# Revit family: 756-102-152-DN150-600
name_source: partatom
category: Pipe Accessories
units: mm (PartAtom-declared; Revit-internal decimal feet)

## family parameters
Always vertical = Yes
Cut with Voids When Loaded = No
Part Type = Valve - Breaks Into
Round Connector Dimension = Use Diameter
Shared = No
Work Plane-Based = No

## types (17) — shared parameters
Body_wallthickness = 10 mm  [stored 0.0328084 ft]
DN150_PN10/16 = 756-0150-1-14102
DN200_PN10 = 756-0200-1-04102
DN200_PN16 = 756-0200-1-14102
DN250_PN10 = 756-0250-1-04102
DN250_PN16 = 756-0250-1-14102
DN300_PN10 = 756-0300-1-04102
DN300_PN16 = 756-0300-1-14102
DN350_PN10 = 756-0350-1-04102
DN350_PN16 = 756-0350-1-14102
DN400_PN10 = 756-0400-1-04102
DN400_PN16 = 756-0400-1-14102
DN450_PN10 = 756-0450-1-04102
DN450_PN16 = 756-0450-1-14102
DN500_PN10 = 756-0500-1-04102
DN500_PN16 = 756-0500-1-14102
DN600_PN10 = 756-0600-1-04102
DN600_PN16 = 756-0600-1-14102
Description_ = AVK DOUBLE ECC. BUTTERFLY VALVE, LONG
GB_Flange = 5 mm  [stored 0.0164042 ft]
Pin_dia = 30 mm  [stored 0.0984252 ft]
RF_Cut_Thickness = 5 mm  [stored 0.0164042 ft]
Rib_depth = 15 mm  [stored 0.0492126 ft]
Search_table = 756-102-152-DN150-600
URL_product_pages = https://www.avkvalves.com

## per-type parameters (varying)
- DN150-PN10/16: A=118 mm; B=224 mm; Bottom_Depth=225 mm; Bottom_width=120 mm; C=181 mm; C_rod=9 mm  [stored 0.0295276 ft]; D1=7.5 mm  [stored 0.0246063 ft]; DN=150 mm; Disc_1=2 mm  [stored 0.00656168 ft]; Disc_2=2 mm  [stored 0.00656168 ft]; Disc_Dia=133 mm; Disc_width=10 mm  [stored 0.0328084 ft]; Flange_OD=142.5 mm; Flange_Thickness=15 mm  [stored 0.0492126 ft]; GB_Dia=35 mm  [stored 0.114829 ft]; GB_Width=76 mm; GB_Width_2=76.5 mm; GB_Width_3=85 mm; Gear_box_Mount_Flange_width=50 mm; Gear_box_Mount_width=43 mm  [stored 0.141076 ft]; Gear_box_depth=83 mm; Gear_box_width=33.5 mm; H1=189 mm; H2=201 mm; H3=230 mm; ID (Radius)=75 mm; L=210 mm; L1=1 mm  [stored 0.00328084 ft]; L2=1 mm  [stored 0.00328084 ft]; Pin_Depth=217.5 mm; Pin_width=105 mm; Rf_Dia=105.5 mm; Rib_height=129.55 mm; Rib_height_2=46.5 mm  [stored 0.152559 ft]; Rib_width=180 mm; Rib_width_2=100 mm; W1=155 mm; W2=287 mm; W3=6 mm  [stored 0.019685 ft]; W4=6 mm  [stored 0.019685 ft]; W5=158 mm; offset=3 mm  [stored 0.00984252 ft]
- DN200_PN10: A=118 mm; B=245 mm; Bottom_Depth=300.15 mm; Bottom_width=140 mm; C=191 mm; C_rod=14 mm  [stored 0.0459318 ft]; D1=7.5 mm  [stored 0.0246063 ft]; DN=200.1 mm; Disc_1=2 mm  [stored 0.00656168 ft]; Disc_2=2 mm  [stored 0.00656168 ft]; Disc_Dia=180 mm; Disc_width=15 mm  [stored 0.0492126 ft]; Flange_OD=170 mm; Flange_Thickness=15 mm  [stored 0.0492126 ft]; GB_Dia=35 mm  [stored 0.114829 ft]; GB_Width=76 mm; GB_Width_2=76.5 mm; GB_Width_3=85 mm; Gear_box_Mount_Flange_width=50 mm; Gear_box_Mount_width=43 mm  [stored 0.141076 ft]; Gear_box_depth=83 mm; Gear_box_width=19.5 mm  [stored 0.0639764 ft]; H1=210 mm; H2=227 mm; H3=240 mm; ID (Radius)=100.05 mm; L=230 mm; L1=1 mm  [stored 0.00328084 ft]; L2=1 mm  [stored 0.00328084 ft]; Pin_Depth=270.05 mm; Pin_width=115 mm; Rf_Dia=133 mm; Rib_height=154.55 mm; Rib_height_2=40 mm  [stored 0.131234 ft]; Rib_width=200 mm; Rib_width_2=100 mm; W1=182 mm; W2=308 mm; W3=6 mm  [stored 0.019685 ft]; W4=6 mm  [stored 0.019685 ft]; W5=158 mm; offset=5 mm  [stored 0.0164042 ft]
- DN200_PN16: A=118 mm; B=245 mm; Bottom_Depth=300.24 mm; Bottom_width=140 mm; C=191 mm; C_rod=14 mm  [stored 0.0459318 ft]; D1=7.5 mm  [stored 0.0246063 ft]; DN=200.16 mm; Disc_1=2 mm  [stored 0.00656168 ft]; Disc_2=2 mm  [stored 0.00656168 ft]; Disc_Dia=180 mm; Disc_width=15 mm  [stored 0.0492126 ft]; Flange_OD=170 mm; Flange_Thickness=15 mm  [stored 0.0492126 ft]; GB_Dia=35 mm  [stored 0.114829 ft]; GB_Width=76 mm; GB_Width_2=76.5 mm; GB_Width_3=85 mm; Gear_box_Mount_Flange_width=50 mm; Gear_box_Mount_width=43 mm  [stored 0.141076 ft]; Gear_box_depth=83 mm; Gear_box_width=28.5 mm  [stored 0.0935039 ft]; H1=210 mm; H2=227 mm; H3=250 mm; ID (Radius)=100.08 mm; L=230 mm; L1=1 mm  [stored 0.00328084 ft]; L2=1 mm  [stored 0.00328084 ft]; Pin_Depth=270.08 mm; Pin_width=115 mm; Rf_Dia=133 mm; Rib_height=154.55 mm; Rib_height_2=40 mm  [stored 0.131234 ft]; Rib_width=200 mm; Rib_width_2=100 mm; W1=182 mm; W2=308 mm; W3=6 mm  [stored 0.019685 ft]; W4=6 mm  [stored 0.019685 ft]; W5=158 mm; offset=5 mm  [stored 0.0164042 ft]
- DN250_PN10: A=118 mm; B=279 mm; Bottom_Depth=375.15 mm; Bottom_width=170 mm; C=201 mm; C_rod=14 mm  [stored 0.0459318 ft]; D1=7.5 mm  [stored 0.0246063 ft]; DN=250.1 mm; Disc_1=2 mm  [stored 0.00656168 ft]; Disc_2=2 mm  [stored 0.00656168 ft]; Disc_Dia=227 mm; Disc_width=15 mm  [stored 0.0492126 ft]; Flange_OD=202.5 mm; Flange_Thickness=15 mm  [stored 0.0492126 ft]; GB_Dia=35 mm  [stored 0.114829 ft]; GB_Width=76 mm; GB_Width_2=76.5 mm; GB_Width_3=85 mm; Gear_box_Mount_Flange_width=45 mm  [stored 0.147638 ft]; Gear_box_Mount_width=37 mm  [stored 0.121391 ft]; Gear_box_depth=83 mm; Gear_box_width=19.5 mm  [stored 0.0639764 ft]; H1=244 mm; H2=261 mm; H3=260 mm; ID (Radius)=125.05 mm; L=250 mm; L1=1 mm  [stored 0.00328084 ft]; L2=1 mm  [stored 0.00328084 ft]; Pin_Depth=327.55 mm; Pin_width=125 mm; Rf_Dia=159.5 mm; Rib_height=184.09 mm; Rib_height_2=41.5 mm  [stored 0.136155 ft]; Rib_width=220 mm; Rib_width_2=90 mm; W1=215 mm; W2=342 mm; W3=6 mm  [stored 0.019685 ft]; W4=6 mm  [stored 0.019685 ft]; W5=158 mm; offset=5 mm  [stored 0.0164042 ft]
- DN250_PN16: A=118 mm; B=279 mm; Bottom_Depth=375.24 mm; Bottom_width=170 mm; C=201 mm; C_rod=14 mm  [stored 0.0459318 ft]; D1=7.5 mm  [stored 0.0246063 ft]; DN=250.16 mm; Disc_1=2 mm  [stored 0.00656168 ft]; Disc_2=2 mm  [stored 0.00656168 ft]; Disc_Dia=227 mm; Disc_width=15 mm  [stored 0.0492126 ft]; Flange_OD=202.5 mm; Flange_Thickness=15 mm  [stored 0.0492126 ft]; GB_Dia=35 mm  [stored 0.114829 ft]; GB_Width=76 mm; GB_Width_2=76.5 mm; GB_Width_3=85 mm; Gear_box_Mount_Flange_width=45 mm  [stored 0.147638 ft]; Gear_box_Mount_width=37 mm  [stored 0.121391 ft]; Gear_box_depth=83 mm; Gear_box_width=19.5 mm  [stored 0.0639764 ft]; H1=244 mm; H2=261 mm; H3=270 mm; ID (Radius)=125.08 mm; L=250 mm; L1=1 mm  [stored 0.00328084 ft]; L2=1 mm  [stored 0.00328084 ft]; Pin_Depth=327.58 mm; Pin_width=125 mm; Rf_Dia=159.5 mm; Rib_height=184.09 mm; Rib_height_2=41.5 mm  [stored 0.136155 ft]; Rib_width=220 mm; Rib_width_2=90 mm; W1=215 mm; W2=342 mm; W3=6 mm  [stored 0.019685 ft]; W4=6 mm  [stored 0.019685 ft]; W5=158 mm; offset=5 mm  [stored 0.0164042 ft]
- DN300_PN10: A=118 mm; B=309 mm; Bottom_Depth=450.15 mm; Bottom_width=210 mm; C=211 mm; C_rod=19 mm  [stored 0.062336 ft]; D1=7.5 mm  [stored 0.0246063 ft]; DN=300.1 mm; Disc_1=3 mm  [stored 0.00984252 ft]; Disc_2=20 mm  [stored 0.0656168 ft]; Disc_Dia=282.17 mm; Disc_width=20 mm  [stored 0.0656168 ft]; Flange_OD=230 mm; Flange_Thickness=20 mm  [stored 0.0656168 ft]; GB_Dia=35 mm  [stored 0.114829 ft]; GB_Width=76 mm; GB_Width_2=76.5 mm; GB_Width_3=85 mm; Gear_box_Mount_Flange_width=55 mm; Gear_box_Mount_width=45 mm  [stored 0.147638 ft]; Gear_box_depth=83 mm; Gear_box_width=27.5 mm  [stored 0.0902231 ft]; H1=274 mm; H2=292 mm; H3=280 mm; ID (Radius)=150.05 mm; L=270 mm; L1=1 mm  [stored 0.00328084 ft]; L2=12 mm  [stored 0.0393701 ft]; Pin_Depth=380.05 mm; Pin_width=135 mm; Rf_Dia=185 mm; Rib_height=209.09 mm; Rib_height_2=44 mm  [stored 0.144357 ft]; Rib_width=230 mm; Rib_width_2=110 mm; W1=242 mm; W2=373 mm; W3=6 mm  [stored 0.019685 ft]; W4=104 mm; W5=182 mm; offset=6 mm  [stored 0.019685 ft]
- DN300_PN16: A=142 mm; B=314 mm; Bottom_Depth=450.24 mm; Bottom_width=210 mm; C=237 mm; C_rod=19 mm  [stored 0.062336 ft]; D1=8.5 mm  [stored 0.0278871 ft]; DN=300.16 mm; Disc_1=3 mm  [stored 0.00984252 ft]; Disc_2=20 mm  [stored 0.0656168 ft]; Disc_Dia=282.17 mm; Disc_width=20 mm  [stored 0.0656168 ft]; Flange_OD=230 mm; Flange_Thickness=20 mm  [stored 0.0656168 ft]; GB_Dia=35 mm  [stored 0.114829 ft]; GB_Width=102 mm; GB_Width_2=103.5 mm; GB_Width_3=115 mm; Gear_box_Mount_Flange_width=55 mm; Gear_box_Mount_width=45 mm  [stored 0.147638 ft]; Gear_box_depth=107 mm; Gear_box_width=32.5 mm  [stored 0.106627 ft]; H1=279 mm; H2=292 mm; H3=290 mm; ID (Radius)=150.08 mm; L=270 mm; L1=1 mm  [stored 0.00328084 ft]; L2=12 mm  [stored 0.0393701 ft]; Pin_Depth=380.08 mm; Pin_width=135 mm; Rf_Dia=185 mm; Rib_height=209.09 mm; Rib_height_2=49 mm; Rib_width=230 mm; Rib_width_2=110 mm; W1=242 mm; W2=373 mm; W3=6 mm  [stored 0.019685 ft]; W4=104 mm; W5=182 mm; offset=6 mm  [stored 0.019685 ft]
- DN350_PN10: A=118 mm; B=335 mm; Bottom_Depth=525.15 mm; Bottom_width=210 mm; C=221 mm; C_rod=19 mm  [stored 0.062336 ft]; D1=7.5 mm  [stored 0.0246063 ft]; DN=350.1 mm; Disc_1=20 mm  [stored 0.0656168 ft]; Disc_2=20 mm  [stored 0.0656168 ft]; Disc_Dia=334 mm; Disc_width=20 mm  [stored 0.0656168 ft]; Flange_OD=260 mm; Flange_Thickness=20 mm  [stored 0.0656168 ft]; GB_Dia=35 mm  [stored 0.114829 ft]; GB_Width=76 mm; GB_Width_2=76.5 mm; GB_Width_3=85 mm; Gear_box_Mount_Flange_width=60 mm; Gear_box_Mount_width=50 mm; Gear_box_depth=83 mm; Gear_box_width=27 mm  [stored 0.0885827 ft]; H1=300 mm; H2=318 mm; H3=300 mm; ID (Radius)=175.05 mm; L=290 mm; L1=20 mm  [stored 0.0656168 ft]; L2=26 mm; Pin_Depth=435.05 mm; Pin_width=145 mm; Rf_Dia=214.5 mm; Rib_height=236.36 mm; Rib_height_2=40 mm  [stored 0.131234 ft]; Rib_width=250 mm; Rib_width_2=120 mm; W1=272 mm; W2=398 mm; W3=151 mm; W4=173 mm; W5=158 mm; offset=3 mm  [stored 0.00984252 ft]
- DN350_PN16: A=142 mm; B=340 mm; Bottom_Depth=525.24 mm; Bottom_width=210 mm; C=247 mm; C_rod=19 mm  [stored 0.062336 ft]; D1=8.5 mm  [stored 0.0278871 ft]; DN=350.16 mm; Disc_1=20 mm  [stored 0.0656168 ft]; Disc_2=20 mm  [stored 0.0656168 ft]; Disc_Dia=334 mm; Disc_width=20 mm  [stored 0.0656168 ft]; Flange_OD=260 mm; Flange_Thickness=20 mm  [stored 0.0656168 ft]; GB_Dia=35 mm  [stored 0.114829 ft]; GB_Width=102 mm; GB_Width_2=76.5 mm; GB_Width_3=85 mm; Gear_box_Mount_Flange_width=60 mm; Gear_box_Mount_width=50 mm; Gear_box_depth=107 mm; Gear_box_width=32 mm  [stored 0.104987 ft]; H1=305 mm; H2=318 mm; H3=310 mm; ID (Radius)=175.08 mm; L=290 mm; L1=20 mm  [stored 0.0656168 ft]; L2=26 mm; Pin_Depth=435.08 mm; Pin_width=145 mm; Rf_Dia=214.5 mm; Rib_height=236.36 mm; Rib_height_2=45 mm  [stored 0.147638 ft]; Rib_width=250 mm; Rib_width_2=120 mm; W1=272 mm; W2=398 mm; W3=151 mm; W4=173 mm; W5=182 mm; offset=3 mm  [stored 0.00984252 ft]
- DN400_PN10: A=142 mm; B=371 mm; Bottom_Depth=600.15 mm; Bottom_width=260 mm; C=257 mm; C_rod=29 mm  [stored 0.0951444 ft]; D1=8.5 mm  [stored 0.0278871 ft]; DN=400.1 mm; Disc_1=20 mm  [stored 0.0656168 ft]; Disc_2=20 mm  [stored 0.0656168 ft]; Disc_Dia=383 mm; Disc_width=30 mm  [stored 0.0984252 ft]; Flange_OD=290 mm; Flange_Thickness=20 mm  [stored 0.0656168 ft]; GB_Dia=37.5 mm; GB_Width=102 mm; GB_Width_2=76.5 mm; GB_Width_3=85 mm; Gear_box_Mount_Flange_width=55 mm; Gear_box_Mount_width=45 mm  [stored 0.147638 ft]; Gear_box_depth=107 mm; Gear_box_width=32 mm  [stored 0.104987 ft]; H1=333.5 mm; H2=349 mm; H3=320 mm; ID (Radius)=200.05 mm; L=310 mm; L1=35 mm  [stored 0.114829 ft]; L2=41 mm  [stored 0.134514 ft]; Pin_Depth=490.05 mm; Pin_width=155 mm; Rf_Dia=240 mm; Rib_height=263.64 mm; Rib_height_2=43.5 mm  [stored 0.142717 ft]; Rib_width=270 mm; Rib_width_2=110 mm; W1=302 mm; W2=434 mm; W3=215 mm; W4=232 mm; W5=182 mm; offset=3 mm  [stored 0.00984252 ft]
- DN400_PN16: A=142 mm; B=371 mm; Bottom_Depth=600.24 mm; Bottom_width=260 mm; C=257 mm; C_rod=29 mm  [stored 0.0951444 ft]; D1=8.5 mm  [stored 0.0278871 ft]; DN=400.16 mm; Disc_1=20 mm  [stored 0.0656168 ft]; Disc_2=20 mm  [stored 0.0656168 ft]; Disc_Dia=383 mm; Disc_width=30 mm  [stored 0.0984252 ft]; Flange_OD=290 mm; Flange_Thickness=20 mm  [stored 0.0656168 ft]; GB_Dia=37.5 mm; GB_Width=102 mm; GB_Width_2=76.5 mm; GB_Width_3=85 mm; Gear_box_Mount_Flange_width=55 mm; Gear_box_Mount_width=45 mm  [stored 0.147638 ft]; Gear_box_depth=107 mm; Gear_box_width=32 mm  [stored 0.104987 ft]; H1=333.5 mm; H2=349 mm; H3=330 mm; ID (Radius)=200.08 mm; L=310 mm; L1=35 mm  [stored 0.114829 ft]; L2=41 mm  [stored 0.134514 ft]; Pin_Depth=490.08 mm; Pin_width=155 mm; Rf_Dia=240 mm; Rib_height=263.64 mm; Rib_height_2=43.5 mm  [stored 0.142717 ft]; Rib_width=270 mm; Rib_width_2=110 mm; W1=302 mm; W2=434 mm; W3=215 mm; W4=232 mm; W5=182 mm; offset=3 mm  [stored 0.00984252 ft]
- DN450_PN10: A=142 mm; B=408 mm; Bottom_Depth=675.15 mm; Bottom_width=280 mm; C=267 mm; C_rod=29 mm  [stored 0.0951444 ft]; D1=8.5 mm  [stored 0.0278871 ft]; DN=450.1 mm; Disc_1=20 mm  [stored 0.0656168 ft]; Disc_2=20 mm  [stored 0.0656168 ft]; Disc_Dia=430 mm; Disc_width=30 mm  [stored 0.0984252 ft]; Flange_OD=320 mm; Flange_Thickness=30 mm  [stored 0.0984252 ft]; GB_Dia=37.5 mm; GB_Width=102 mm; GB_Width_2=98.1 mm; GB_Width_3=109 mm; Gear_box_Mount_Flange_width=67.5 mm; Gear_box_Mount_width=58 mm; Gear_box_depth=107 mm; Gear_box_width=28 mm  [stored 0.0918635 ft]; H1=370.5 mm; H2=390 mm; H3=340 mm; ID (Radius)=225.05 mm; L=330 mm; L1=48 mm  [stored 0.15748 ft]; L2=55 mm; Pin_Depth=545.05 mm; Pin_width=165 mm; Rf_Dia=265 mm; Rib_height=290.91 mm; Rib_height_2=50.5 mm; Rib_width=270 mm; Rib_width_2=135 mm; W1=332 mm; W2=471 mm; W3=267 mm; W4=284 mm; W5=182 mm; offset=3 mm  [stored 0.00984252 ft]
- DN450_PN16: A=186 mm; B=423 mm; Bottom_Depth=675.24 mm; Bottom_width=280 mm; C=301 mm; C_rod=29 mm  [stored 0.0951444 ft]; D1=12.5 mm  [stored 0.0410105 ft]; DN=450.16 mm; Disc_1=20 mm  [stored 0.0656168 ft]; Disc_2=20 mm  [stored 0.0656168 ft]; Disc_Dia=430 mm; Disc_width=30 mm  [stored 0.0984252 ft]; Flange_OD=320 mm; Flange_Thickness=30 mm  [stored 0.0984252 ft]; GB_Dia=37.5 mm; GB_Width=136 mm; GB_Width_2=98.1 mm; GB_Width_3=109 mm; Gear_box_Mount_Flange_width=67.5 mm; Gear_box_Mount_width=58 mm; Gear_box_depth=151 mm; Gear_box_width=43 mm  [stored 0.141076 ft]; H1=385.5 mm; H2=390 mm; H3=350 mm; ID (Radius)=225.08 mm; L=330 mm; L1=48 mm  [stored 0.15748 ft]; L2=55 mm; Pin_Depth=545.08 mm; Pin_width=165 mm; Rf_Dia=265 mm; Rib_height=290.91 mm; Rib_height_2=65.5 mm; Rib_width=270 mm; Rib_width_2=135 mm; W1=332 mm; W2=471 mm; W3=267 mm; W4=284 mm; W5=236 mm; offset=3 mm  [stored 0.00984252 ft]
- DN500_PN10: A=142 mm; B=436 mm; Bottom_Depth=750.15 mm; Bottom_width=320 mm; C=277 mm; C_rod=34 mm; D1=8.5 mm  [stored 0.0278871 ft]; DN=500.1 mm; Disc_1=20 mm  [stored 0.0656168 ft]; Disc_2=20 mm  [stored 0.0656168 ft]; Disc_Dia=480.61 mm; Disc_width=35 mm  [stored 0.114829 ft]; Flange_OD=335 mm; Flange_Thickness=30 mm  [stored 0.0984252 ft]; GB_Dia=39 mm  [stored 0.127953 ft]; GB_Width=102 mm; GB_Width_2=98.1 mm; GB_Width_3=109 mm; Gear_box_Mount_Flange_width=67.5 mm; Gear_box_Mount_width=58 mm; Gear_box_depth=107 mm; Gear_box_width=19 mm  [stored 0.062336 ft]; H1=397 mm; H2=418 mm; H3=360 mm; ID (Radius)=250.05 mm; L=350 mm; L1=63 mm; L2=69 mm; Pin_Depth=585.05 mm; Pin_width=175 mm; Rf_Dia=291 mm; Rib_height=304.55 mm; Rib_height_2=62 mm; Rib_width=290 mm; Rib_width_2=135 mm; W1=338 mm; W2=499 mm; W3=322 mm; W4=335 mm; W5=182 mm; offset=3 mm  [stored 0.00984252 ft]
- DN500_PN16: A=186 mm; B=460 mm; Bottom_Depth=750.24 mm; Bottom_width=320 mm; C=311 mm; C_rod=34 mm; D1=12.5 mm  [stored 0.0410105 ft]; DN=500.16 mm; Disc_1=20 mm  [stored 0.0656168 ft]; Disc_2=20 mm  [stored 0.0656168 ft]; Disc_Dia=480.61 mm; Disc_width=35 mm  [stored 0.114829 ft]; Flange_OD=335 mm; Flange_Thickness=30 mm  [stored 0.0984252 ft]; GB_Dia=39 mm  [stored 0.127953 ft]; GB_Width=136 mm; GB_Width_2=98.1 mm; GB_Width_3=109 mm; Gear_box_Mount_Flange_width=67.5 mm; Gear_box_Mount_width=58 mm; Gear_box_depth=151 mm; Gear_box_width=43 mm  [stored 0.141076 ft]; H1=421 mm; H2=427 mm; H3=370 mm; ID (Radius)=250.08 mm; L=350 mm; L1=63 mm; L2=69 mm; Pin_Depth=585.08 mm; Pin_width=175 mm; Rf_Dia=291 mm; Rib_height=304.55 mm; Rib_height_2=86 mm; Rib_width=290 mm; Rib_width_2=135 mm; W1=370 mm; W2=550 mm; W3=322 mm; W4=335 mm; W5=236 mm; offset=3 mm  [stored 0.00984252 ft]
- DN600_PN10: A=186 mm; B=510 mm; Bottom_Depth=900.15 mm; Bottom_width=400 mm; C=331 mm; C_rod=39 mm  [stored 0.127953 ft]; D1=12.5 mm  [stored 0.0410105 ft]; DN=600.1 mm; Disc_1=20 mm  [stored 0.0656168 ft]; Disc_2=20 mm  [stored 0.0656168 ft]; Disc_Dia=582 mm; Disc_width=40 mm  [stored 0.131234 ft]; Flange_OD=390 mm; Flange_Thickness=30 mm  [stored 0.0984252 ft]; GB_Dia=39 mm  [stored 0.127953 ft]; GB_Width=136 mm; GB_Width_2=108 mm; GB_Width_3=120 mm; Gear_box_Mount_Flange_width=77.5 mm; Gear_box_Mount_width=62.5 mm; Gear_box_depth=151 mm; Gear_box_width=28 mm  [stored 0.0918635 ft]; H1=471 mm; H2=481 mm; H3=380 mm; ID (Radius)=300.05 mm; L=390 mm; L1=94 mm; L2=100 mm; Pin_Depth=690.05 mm; Pin_width=195 mm; Rf_Dia=341 mm; Rib_height=354.55 mm; Rib_height_2=81 mm; Rib_width=330 mm; Rib_width_2=155 mm; W1=393 mm; W2=600 mm; W3=426 mm; W4=437 mm; W5=236 mm; offset=3 mm  [stored 0.00984252 ft]
- DN600_PN16: A=313 mm; B=532 mm; Bottom_Depth=900.24 mm; Bottom_width=400 mm; C=267 mm; C_rod=39 mm  [stored 0.127953 ft]; D1=10 mm  [stored 0.0328084 ft]; DN=600.16 mm; Disc_1=20 mm  [stored 0.0656168 ft]; Disc_2=20 mm  [stored 0.0656168 ft]; Disc_Dia=582 mm; Disc_width=40 mm  [stored 0.131234 ft]; Flange_OD=390 mm; Flange_Thickness=30 mm  [stored 0.0984252 ft]; GB_Dia=39 mm  [stored 0.127953 ft]; GB_Width=72 mm; GB_Width_2=108 mm; GB_Width_3=120 mm; Gear_box_Mount_Flange_width=77.5 mm; Gear_box_Mount_width=62.5 mm; Gear_box_depth=278 mm; Gear_box_width=39 mm  [stored 0.127953 ft]; H1=493 mm; H2=503 mm; H3=390 mm; ID (Radius)=300.08 mm; L=390 mm; L1=94 mm; L2=100 mm; Pin_Depth=690.08 mm; Pin_width=195 mm; Rf_Dia=341 mm; Rib_height=354.55 mm; Rib_height_2=103 mm; Rib_width=330 mm; Rib_width_2=155 mm; W1=435 mm; W2=627 mm; W3=426 mm; W4=437 mm; W5=364 mm; offset=3 mm  [stored 0.00984252 ft]

note: [stored X ft] marks values corroborated as IEEE doubles in the binary element streams (Revit-internal decimal feet)

## geometry (parser evidence)
native form markers: Sweep x9
no freeform markers — native parametric forms only
